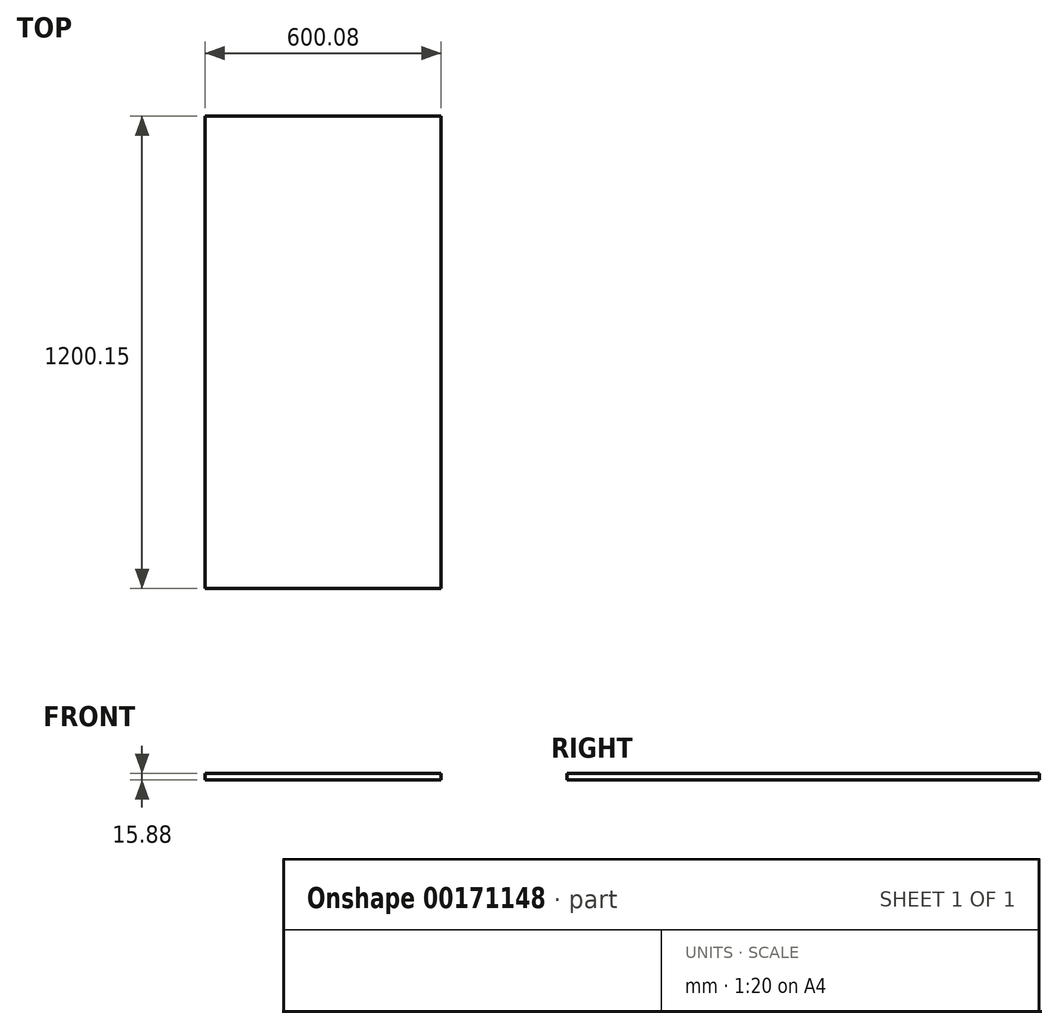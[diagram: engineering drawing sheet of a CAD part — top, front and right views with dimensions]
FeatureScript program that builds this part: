
annotation { "Feature Type Name" : "Feature", "Feature Type Description" : "" }
export const myFeature = defineFeature(function(context is Context, id is Id, definition is map)
    precondition{}
    {
        {
            var Q0;
            Q0=qCreatedBy(makeId("Front.planeOp"),FACE);
            var sketch = newSketch(context, id + "F0", { "sketchPlane" : qUnion([Q0])});
            skLineSegment(sketch, "E0", {"start": v(0, 0) * mm, "end": v(-300.04, 0) * mm});
            skLineSegment(sketch, "E1", {"start": v(-300.04, 0) * mm, "end": v(-300.04, -15.88) * mm});
            skLineSegment(sketch, "E2", {"start": v(-300.04, -15.88) * mm, "end": v(300.04, -15.88) * mm});
            skLineSegment(sketch, "E3", {"start": v(300.04, -15.88) * mm, "end": v(300.04, 0) * mm});
            skLineSegment(sketch, "E4", {"start": v(300.04, 0) * mm, "end": v(0, 0) * mm});
            skSolve(sketch);
        }
        {
            var Q0;
            Q0=makeQuery(id+"F0.imprint","IMPRINT",FACE,{"disambiguationData":[TD([[makeQuery(id+"F0.imprint","IMPRINT",EDGE,{"derivedFrom":sQuery(id+"F0.wireOp",EDGE,"E0")}),1.0]])]});
            extrude(context, id + "F1", {"entities" : qUnion([Q0]), "oppositeDirection" : true, "depth" : 1200.15 * mm});
        }
    });
